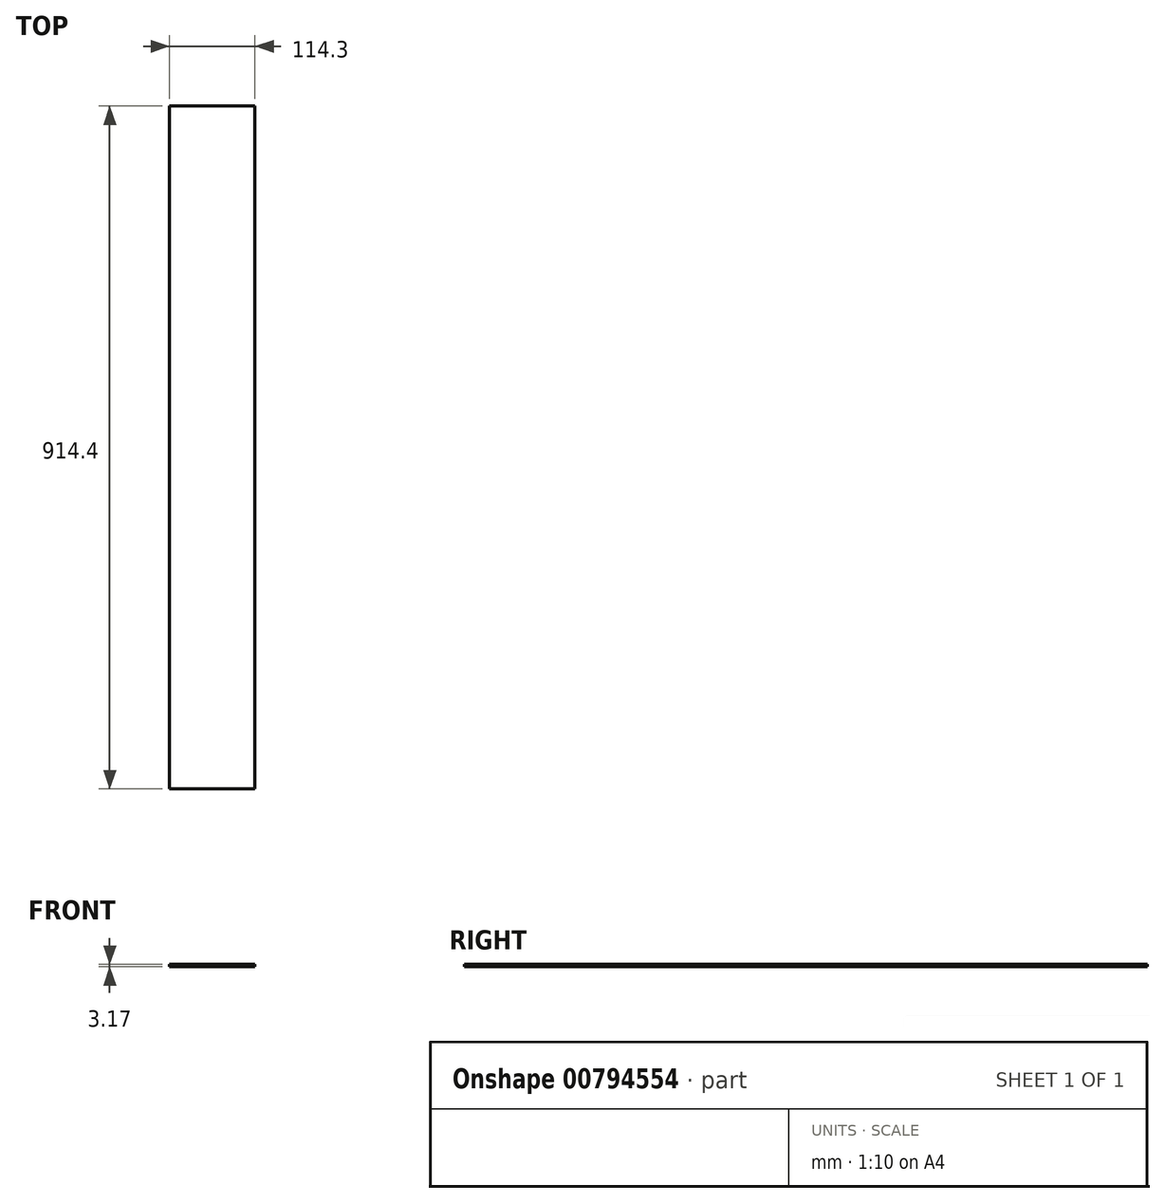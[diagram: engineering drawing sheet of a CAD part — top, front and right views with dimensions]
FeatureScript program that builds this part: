
annotation { "Feature Type Name" : "Feature", "Feature Type Description" : "" }
export const myFeature = defineFeature(function(context is Context, id is Id, definition is map)
    precondition{}
    {
        {
            var Q0;
            Q0=qCreatedBy(makeId("Top.planeOp"),FACE);
            var sketch = newSketch(context, id + "F0", { "sketchPlane" : qUnion([Q0])});
            skLineSegment(sketch, "E0.bottom", {"start": v(-310.43, -477.17) * mm, "end": v(-424.73, -477.17) * mm});
            skLineSegment(sketch, "E0.top", {"start": v(-310.43, 437.23) * mm, "end": v(-424.73, 437.23) * mm});
            skLineSegment(sketch, "E0.left", {"start": v(-310.43, -477.17) * mm, "end": v(-310.43, 437.23) * mm});
            skLineSegment(sketch, "E0.right", {"start": v(-424.73, -477.17) * mm, "end": v(-424.73, 437.23) * mm});
            skSolve(sketch);
        }
        {
            var Q0;
            Q0=qSketchRegion(id+"F0",true);
            extrude(context, id + "F1", {"entities" : qUnion([Q0]), "depth" : 3.17 * mm, "offsetDistance" : 25.4 * mm});
        }
    });
